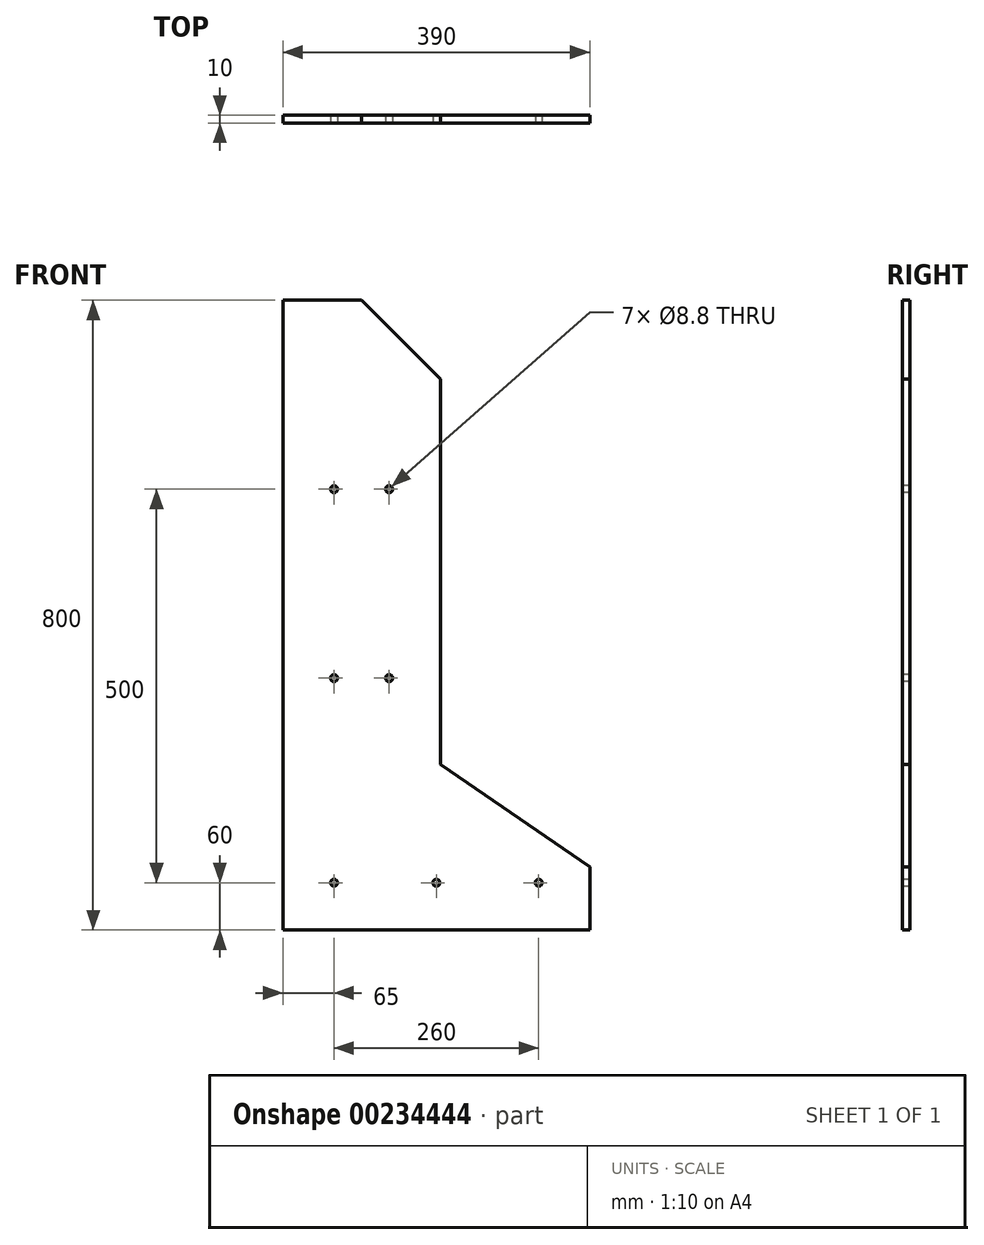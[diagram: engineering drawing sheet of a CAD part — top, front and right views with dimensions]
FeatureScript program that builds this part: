
annotation { "Feature Type Name" : "Feature", "Feature Type Description" : "" }
export const myFeature = defineFeature(function(context is Context, id is Id, definition is map)
    precondition{}
    {
        {
            var Q0;
            Q0=qCreatedBy(makeId("Front.planeOp"),FACE);
            var sketch = newSketch(context, id + "F0", { "sketchPlane" : qUnion([Q0])});
            skLineSegment(sketch, "E0.bottom", {"start": v(195, 400) * mm, "end": v(-195, 400) * mm});
            skLineSegment(sketch, "E0.top", {"start": v(195, -400) * mm, "end": v(-195, -400) * mm});
            skLineSegment(sketch, "E0.left", {"start": v(195, 400) * mm, "end": v(195, -400) * mm});
            skLineSegment(sketch, "E0.right", {"start": v(-195, 400) * mm, "end": v(-195, -400) * mm});
            skPoint(sketch, "E0.middle", {"position": v(0, 0) * mm});
            skSolve(sketch);
        }
        {
            var Q0;
            Q0 = qSketchRegion(id + "F0", true);
            extrude(context, id + "F1", {"entities" : qUnion([Q0]), "depth" : 10 * mm});
        }
        {
            var Q0;
            Q0=makeQuery(id+"F1.opExtrude","CAP_FACE",FACE,{"disambiguationData":[OSD([sQuery(id+"F0.wireOp",EDGE,"E0.bottom"),sQuery(id+"F0.wireOp",EDGE,"E0.top"),sQuery(id+"F0.wireOp",EDGE,"E0.left"),sQuery(id+"F0.wireOp",EDGE,"E0.right")])],"isStart":false});
            var sketch = newSketch(context, id + "F2", { "sketchPlane" : qUnion([Q0])});
            skLineSegment(sketch, "E1", {"start": v(195, -320) * mm, "end": v(5, -190) * mm});
            skLineSegment(sketch, "E2", {"start": v(5, -190) * mm, "end": v(5, 300) * mm});
            skLineSegment(sketch, "E3", {"start": v(-95, 400) * mm, "end": v(5, 300) * mm});
            skSolve(sketch);
        }
        {
            var Q0;
            {var subQ0=sQuery(id+"F2.wireOp",EDGE,"E1");Q0=makeQuery(id+"F2.imprint","IMPRINT",FACE,{"disambiguationData":[TD([[makeQuery(id+"F2.imprint","IMPRINT",EDGE,{"derivedFrom":subQ0}),-1.0]])]});}
            extrude(context, id + "F3", {"entities" : qUnion([Q0]), "operationType" : NewBodyOperationType.REMOVE, "oppositeDirection" : true, "depth" : 25 * mm});
        }
        {
            var Q0;
            Q0=makeQuery(id+"F1.opExtrude","CAP_FACE",FACE,{"disambiguationData":[OSD([sQuery(id+"F0.wireOp",EDGE,"E0.bottom"),sQuery(id+"F0.wireOp",EDGE,"E0.top"),sQuery(id+"F0.wireOp",EDGE,"E0.left"),sQuery(id+"F0.wireOp",EDGE,"E0.right")])],"isStart":false});
            var sketch = newSketch(context, id + "F4", { "sketchPlane" : qUnion([Q0])});
            skLineSegment(sketch, "E4", {"start": v(195, -340) * mm, "end": v(-195, -340) * mm, "construction": true});
            skLineSegment(sketch, "E5", {"start": v(5, -80) * mm, "end": v(-195, -80) * mm, "construction": true});
            skLineSegment(sketch, "E6", {"start": v(5, 160) * mm, "end": v(-195, 160) * mm, "construction": true});
            skPoint(sketch, "E7", {"position": v(-130, 160) * mm});
            skPoint(sketch, "E8", {"position": v(-60, 160) * mm});
            skPoint(sketch, "E9", {"position": v(-60, -80) * mm});
            skPoint(sketch, "E10", {"position": v(0, -340) * mm});
            skPoint(sketch, "E11", {"position": v(130, -340) * mm});
            skPoint(sketch, "E12", {"position": v(-130, -340) * mm});
            skPoint(sketch, "E13", {"position": v(-130, -80) * mm});
            skLineSegment(sketch, "E14", {"start": v(-130, 160) * mm, "end": v(-130, -80) * mm, "construction": true});
            skLineSegment(sketch, "E15", {"start": v(-60, 160) * mm, "end": v(-60, -80) * mm, "construction": true});
            skLineSegment(sketch, "E16", {"start": v(-195, 40) * mm, "end": v(-130, 40) * mm, "construction": true});
            skLineSegment(sketch, "E17", {"start": v(-60, 40) * mm, "end": v(5, 40) * mm, "construction": true});
            skLineSegment(sketch, "E18", {"start": v(-130, 40) * mm, "end": v(-60, 40) * mm, "construction": true});
            skSolve(sketch);
        }
        {
            var Q0;
            Q0=sQuery(id+"F4.wireOp",VERTEX,"E7");
            var Q1;
            Q1=sQuery(id+"F4.wireOp",VERTEX,"E8");
            var Q2;
            Q2=sQuery(id+"F4.wireOp",VERTEX,"E13");
            var Q3;
            Q3=sQuery(id+"F4.wireOp",VERTEX,"E9");
            var Q4;
            Q4=sQuery(id+"F4.wireOp",VERTEX,"E12");
            var Q5;
            Q5=sQuery(id+"F4.wireOp",VERTEX,"E10");
            var Q6;
            Q6=sQuery(id+"F4.wireOp",VERTEX,"E11");
            var Q7;
            Q7=makeQuery(id+"F1.opExtrude","SWEPT_BODY",BODY,{"disambiguationData":[OSD([sQuery(id+"F0.wireOp",EDGE,"E0.bottom"),sQuery(id+"F0.wireOp",EDGE,"E0.top"),sQuery(id+"F0.wireOp",EDGE,"E0.left"),sQuery(id+"F0.wireOp",EDGE,"E0.right")])]});
            hole(context, id + "F5", {"style" : HoleStyle.SIMPLE, "endStyle" : HoleEndStyle.THROUGH, "standardTappedOrClearance" : lookupTablePath({ "standard" : "ISO", "fit" : "Normal", "size" : "M8", "type" : "Clearance" }), "standardBlindInLast" : lookupTablePath({ "fit" : "Standard", "standard" : "ISO", "size" : "M8", "type" : "Clearance" }), "holeDiameter" : 8.8 * mm, "locations" : qUnion([Q0, Q1, Q2, Q3, Q4, Q5, Q6]), "scope" : qUnion([Q7]), "isTappedThrough" : true});
        }
    });
